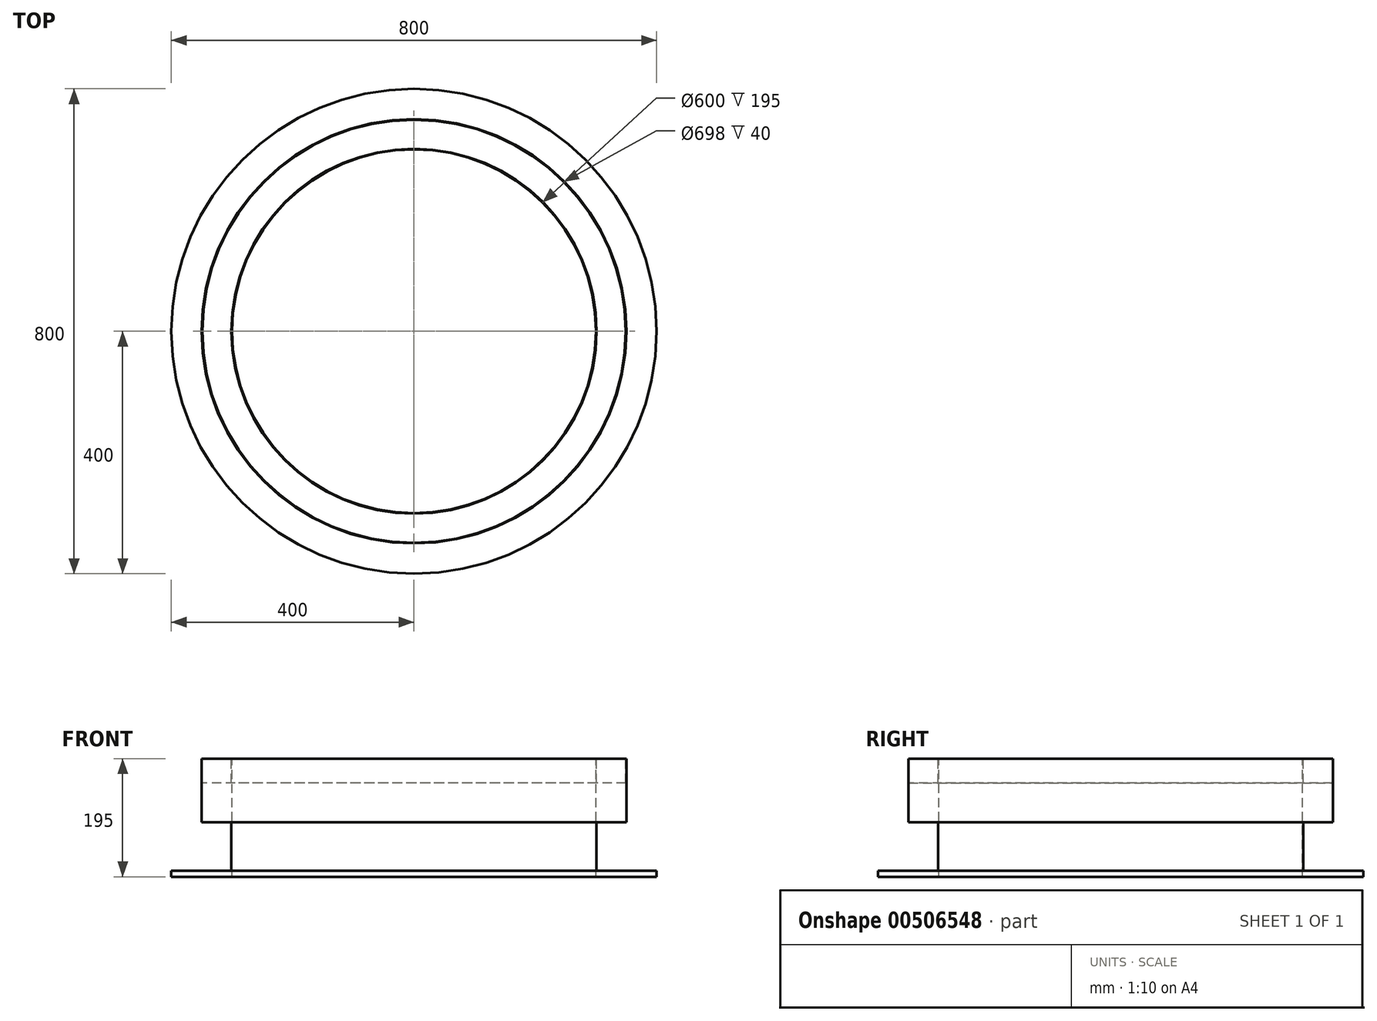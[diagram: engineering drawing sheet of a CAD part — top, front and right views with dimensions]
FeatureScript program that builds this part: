
annotation { "Feature Type Name" : "Feature", "Feature Type Description" : "" }
export const myFeature = defineFeature(function(context is Context, id is Id, definition is map)
    precondition{}
    {
        {
            var Q0;
            Q0=qCreatedBy(makeId("Front.planeOp"),FACE);
            var sketch = newSketch(context, id + "F0", { "sketchPlane" : qUnion([Q0])});
            skLineSegment(sketch, "E0", {"start": v(0, 710.75) * mm, "end": v(0, -704.58) * mm, "construction": true});
            skLineSegment(sketch, "E1", {"start": v(-300, 300.65) * mm, "end": v(-300, 495.65) * mm});
            skLineSegment(sketch, "E2", {"start": v(-300, 495.65) * mm, "end": v(-301, 495.65) * mm});
            skLineSegment(sketch, "E3", {"start": v(-349, 495.65) * mm, "end": v(-350, 495.65) * mm});
            skLineSegment(sketch, "E4", {"start": v(-350, 495.65) * mm, "end": v(-350, 390.65) * mm});
            skLineSegment(sketch, "E5", {"start": v(-350, 390.65) * mm, "end": v(-301, 390.65) * mm});
            skLineSegment(sketch, "E6", {"start": v(-301, 390.65) * mm, "end": v(-301, 310.65) * mm});
            skLineSegment(sketch, "E7", {"start": v(-301, 310.65) * mm, "end": v(-400, 310.65) * mm});
            skLineSegment(sketch, "E8", {"start": v(-400, 310.65) * mm, "end": v(-400, 300.65) * mm});
            skLineSegment(sketch, "E9", {"start": v(-400, 300.65) * mm, "end": v(-300, 300.65) * mm});
            skLineSegment(sketch, "E10", {"start": v(-349, 495.65) * mm, "end": v(-349, 455.65) * mm});
            skLineSegment(sketch, "E11", {"start": v(-349, 455.65) * mm, "end": v(-301, 455.65) * mm});
            skLineSegment(sketch, "E12", {"start": v(-301, 455.65) * mm, "end": v(-301, 495.65) * mm});
            skSolve(sketch);
        }
        {
            var Q0;
            Q0=qSketchRegion(id+"F0",true);
            var Q1;
            Q1=sQuery(id+"F0.wireOp",EDGE,"E0");
            revolve(context, id + "F1", {"entities" : qUnion([Q0]), "axis" : qUnion([Q1]), "revolveType" : RevolveType.FULL});
        }
    });
